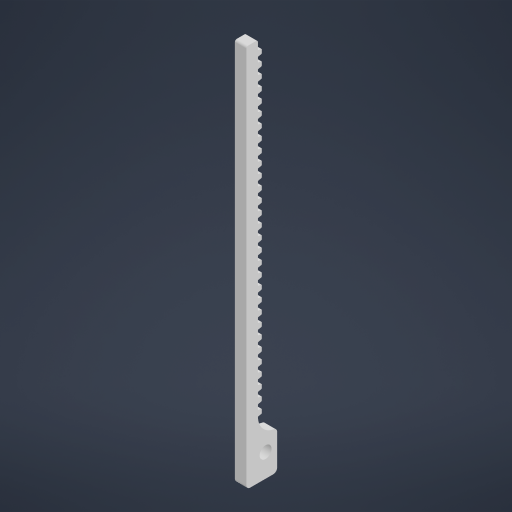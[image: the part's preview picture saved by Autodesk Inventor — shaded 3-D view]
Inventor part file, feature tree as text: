
AUTODESK INVENTOR PART (.ipt)
format: ipt  version: 2023 (Build 270158000, 158)  size: 564,224 bytes
history: native  units: mm
features: extrude x2, sketch x2, fillet x1
ambient origin geometry x8: Origin, YZ Plane, XZ Plane, XY Plane, X Axis, Y Axis, Z Axis, Center Point
bodies: Solid1 (feature_tree)
feature tree (5):
  extrude  "Extrusion1"  Depth=8.0mm
  fillet  "Fillet1"  Radius=90.0mm
  extrude  "Extrusion2"  Depth=3.0mm TaperAngle=0.0deg
  sketch  "Sketch1"  dims[d0=10.0mm d1=8.0mm d2=90.0mm]
  sketch  "Sketch3"  dims[d3=3.0mm d4=3.0mm d5=0.0mm d6=3.1mm d7=5.0mm d8=4.0mm d9=5.0mm d10=1.0mm d11=0.5mm d12=1.0mm d13=0.75mm d14=0.2mm d15=0.1mm d16=0.1mm d17=300.0mm d19=2.8mm d20=10.0mm d22=10.0mm d24=10.0mm d25=0.0mm]
